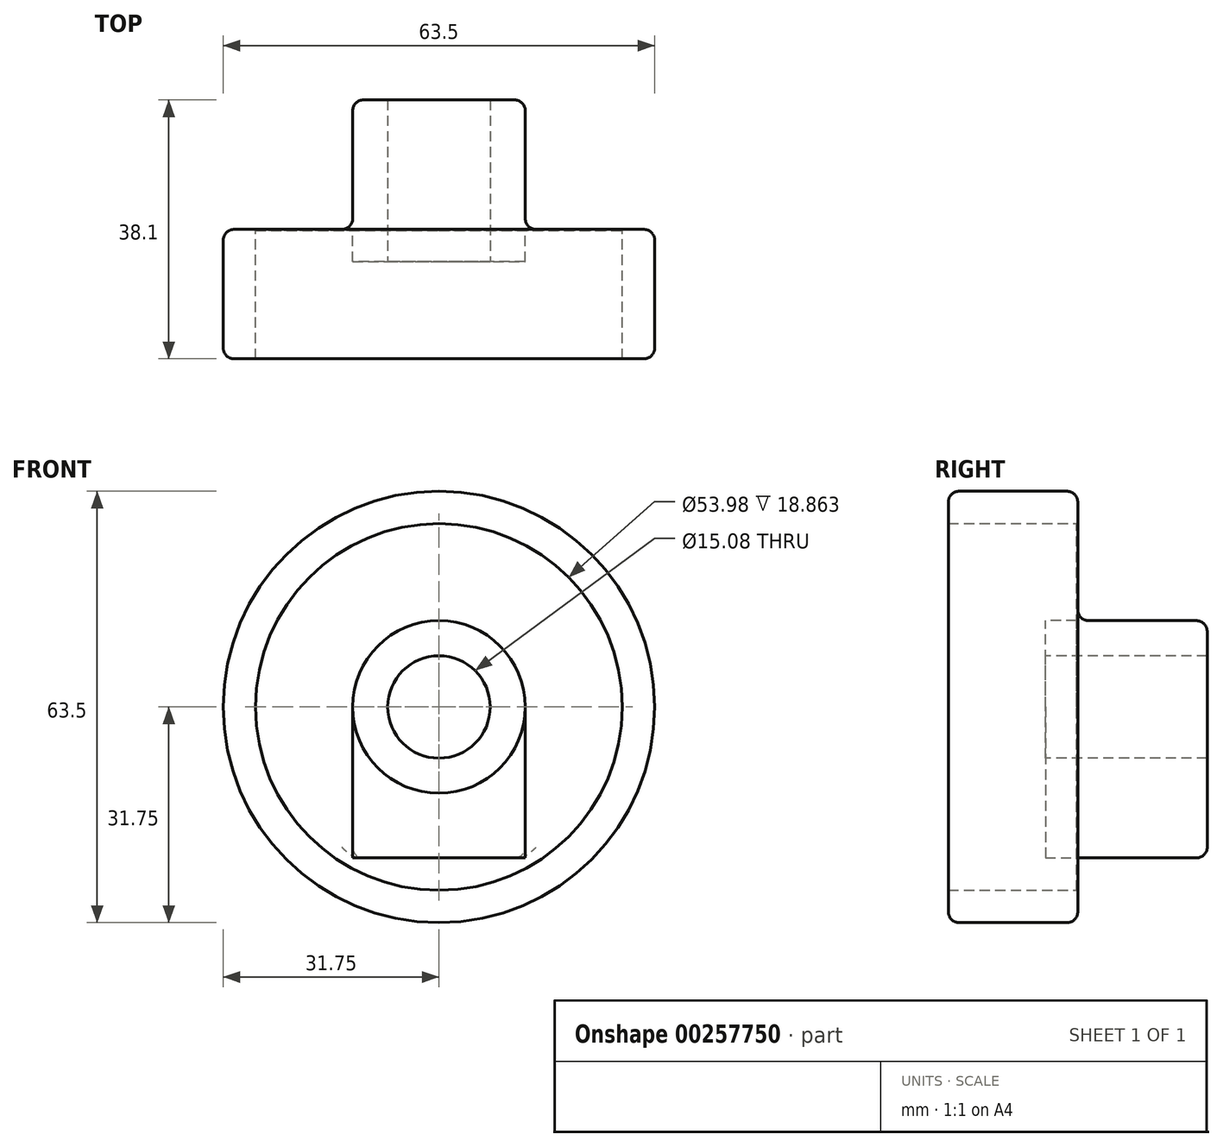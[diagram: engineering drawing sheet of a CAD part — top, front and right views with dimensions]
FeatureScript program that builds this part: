
annotation { "Feature Type Name" : "Feature", "Feature Type Description" : "" }
export const myFeature = defineFeature(function(context is Context, id is Id, definition is map)
    precondition{}
    {
        {
            var Q0;
            Q0=qCreatedBy(makeId("Front.planeOp"),FACE);
            var sketch = newSketch(context, id + "F0", { "sketchPlane" : qUnion([Q0])});
            skCircle(sketch, "E0", {"center": v(0, 0) * mm, "radius": 31.75 * mm});
            skCircle(sketch, "E1", {"center": v(0, 0) * mm, "radius": 26.99 * mm});
            skCircle(sketch, "E2", {"center": v(0, 0) * mm, "radius": 7.54 * mm});
            skCircle(sketch, "E3", {"center": v(0, 0) * mm, "radius": 12.7 * mm});
            skLineSegment(sketch, "E4", {"start": v(12.7, 0) * mm, "end": v(-12.7, 0) * mm, "construction": true});
            skLineSegment(sketch, "E5", {"start": v(12.7, 0) * mm, "end": v(12.7, -22.23) * mm});
            skLineSegment(sketch, "E6", {"start": v(-12.7, 0) * mm, "end": v(-12.7, -22.23) * mm});
            skLineSegment(sketch, "E7", {"start": v(12.7, -22.23) * mm, "end": v(-12.7, -22.23) * mm});
            skSolve(sketch);
        }
        {
            var Q0;
            Q0 = qSketchRegion(id + "F0", true);
            extrude(context, id + "F1", {"entities" : qUnion([Q0]), "depth" : 19.05 * mm});
        }
        {
            var Q0;
            Q0=makeQuery(id+"F0.imprint","IMPRINT",FACE,{"disambiguationData":[TD([[makeQuery(id+"F0.imprint","IMPRINT",EDGE,{"derivedFrom":sQuery(id+"F0.wireOp",EDGE,"E1")}),1.0]])]});
            extrude(context, id + "F2", {"entities" : qUnion([Q0]), "operationType" : NewBodyOperationType.ADD, "depth" : ((3 / 4) - (9 / 16)) * mm});
        }
        {
            var Q0;
            Q0=makeQuery(id+"F0.imprint","IMPRINT",FACE,{"disambiguationData":[TD([[makeQuery(id+"F0.imprint","IMPRINT",EDGE,{"derivedFrom":sQuery(id+"F0.wireOp",EDGE,"E2")}),-1.0]])]});
            extrude(context, id + "F3", {"entities" : qUnion([Q0]), "operationType" : NewBodyOperationType.ADD, "oppositeDirection" : true, "depth" : 19.05 * mm});
        }
        {
            var Q0;
            Q0=makeQuery(id+"F3.opExtrude","CAP_FACE",FACE,{"disambiguationData":[OSD([sQuery(id+"F0.wireOp",EDGE,"E2"),sQuery(id+"F0.wireOp",EDGE,"E3")])],"isStart":true});
            extrude(context, id + "F4", {"entities" : qUnion([Q0]), "operationType" : NewBodyOperationType.ADD, "depth" : 4.76 * mm});
        }
        {
            var Q0;
            {var subQ0=sQuery(id+"F0.wireOp",EDGE,"E5");Q0=makeQuery(id+"F0.imprint","IMPRINT",FACE,{"disambiguationData":[TD([[makeQuery(id+"F0.imprint","IMPRINT",EDGE,{"derivedFrom":subQ0}),-1.0]])]});}
            extrude(context, id + "F5", {"entities" : qUnion([Q0]), "operationType" : NewBodyOperationType.ADD, "depth" : 4.78 * mm});
        }
        {
            var Q0;
            {var subQ0=sQuery(id+"F0.wireOp",EDGE,"E5");Q0=makeQuery(id+"F0.imprint","IMPRINT",FACE,{"disambiguationData":[TD([[makeQuery(id+"F0.imprint","IMPRINT",EDGE,{"derivedFrom":subQ0}),-1.0]])]});}
            extrude(context, id + "F6", {"entities" : qUnion([Q0]), "operationType" : NewBodyOperationType.ADD, "oppositeDirection" : true, "depth" : 19.05 * mm});
        }
        {
            var Q0;
            Q0=makeQuery(id+"F1.opExtrude","CAP_EDGE",EDGE,{"disambiguationData":[OSD([sQuery(id+"F0.wireOp",EDGE,"E0")])],"isStart":false});
            var Q1;
            Q1=makeQuery(id+"F1.opExtrude","CAP_EDGE",EDGE,{"disambiguationData":[OSD([sQuery(id+"F0.wireOp",EDGE,"E0")])],"isStart":true});
            var Q2;
            Q2=makeQuery(id+"F3.opExtrude","CAP_EDGE",EDGE,{"disambiguationData":[OSD([sQuery(id+"F0.wireOp",EDGE,"E3")])],"isStart":false});
            fillet(context, id + "F7", {"entities" : qUnion([Q0, Q1, Q2]), "radius" : 1.59 * mm, "tangentPropagation" : true, "allowEdgeOverflow" : false});
        }
        {
            var Q0;
            {var subQ0=sQuery(id+"F0.wireOp",EDGE,"E3");Q0=makeQuery(id+"F5.boolean.opBoolean","MERGE",EDGE,{"derivedFrom":[makeQuery(id+"F2.opExtrude","CAP_EDGE",EDGE,{"disambiguationData":[OSD([subQ0])],"isStart":true}),makeQuery(id+"F5.opExtrude","CAP_EDGE",EDGE,{"disambiguationData":[OSD([subQ0])],"isStart":true})]});}
            fillet(context, id + "F8", {"entities" : qUnion([Q0]), "radius" : 1.59 * mm, "tangentPropagation" : true, "allowEdgeOverflow" : false});
        }
        {
            var Q0;
            Q0=makeQuery(id+"F6.opExtrude","SWEPT_EDGE",EDGE,{"disambiguationData":[OSD([sQuery(id+"F0.wireOp",EDGE,"E5"),sQuery(id+"F0.wireOp",EDGE,"E7")])]});
            var Q1;
            Q1=makeQuery(id+"F6.opExtrude","CAP_EDGE",EDGE,{"disambiguationData":[OSD([sQuery(id+"F0.wireOp",EDGE,"E7")])],"isStart":false});
            fillet(context, id + "F9", {"entities" : qUnion([Q0, Q1]), "radius" : 1.59 * mm, "tangentPropagation" : true, "allowEdgeOverflow" : false});
        }
    });
